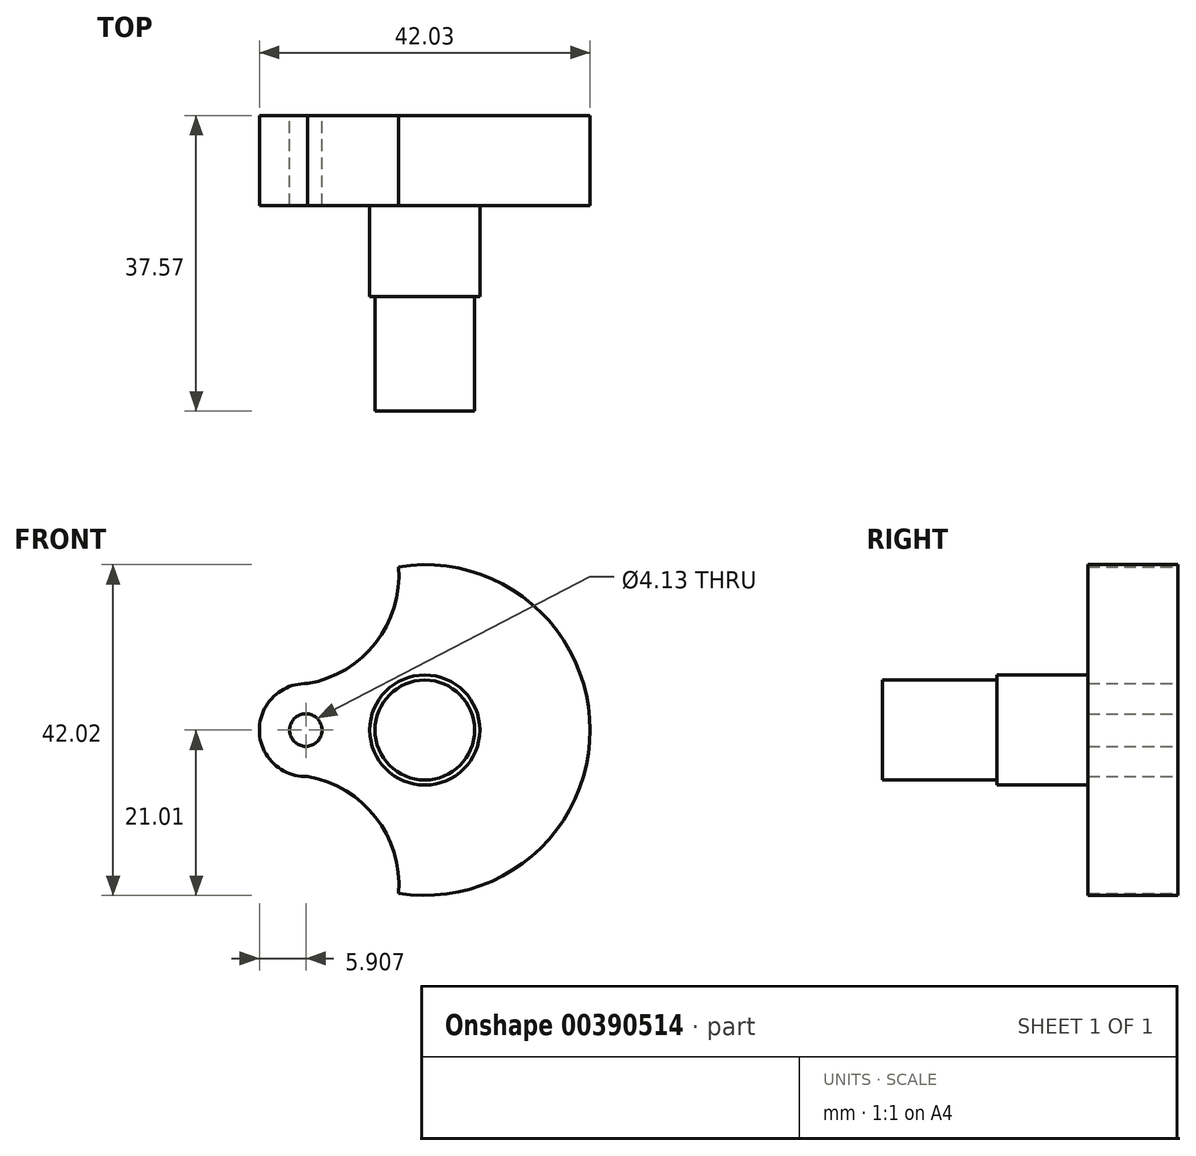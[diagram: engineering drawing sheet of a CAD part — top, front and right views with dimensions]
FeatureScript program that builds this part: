
annotation { "Feature Type Name" : "Feature", "Feature Type Description" : "" }
export const myFeature = defineFeature(function(context is Context, id is Id, definition is map)
    precondition{}
    {
        {
            var Q0;
            Q0=qCreatedBy(makeId("Front.planeOp"),FACE);
            var sketch = newSketch(context, id + "F0", { "sketchPlane" : qUnion([Q0])});
            skArc(sketch, "E0", {"start": v(-3.32, -20.74) * mm, "mid": v(21, 0) * mm, "end": v(-3.32, 20.74) * mm});
            skPoint(sketch, "E1", {"position": v(-15.11, 0) * mm});
            skArc(sketch, "E2", {"start": v(-14.89, 5.9) * mm, "mid": v(-21.02, 0) * mm, "end": v(-14.89, -5.9) * mm});
            skArc(sketch, "E3", {"start": v(-3.32, -20.74) * mm, "mid": v(-6.8, -10.42) * mm, "end": v(-16.61, -5.71) * mm});
            skPoint(sketch, "E3.first.point", {"position": v(-14.89, -5.9) * mm});
            skPoint(sketch, "E3.second.point", {"position": v(-12.16, -32.72) * mm});
            skPoint(sketch, "E3.third.point", {"position": v(-16.61, -5.71) * mm});
            skArc(sketch, "E4.MirrorCS", {"start": v(-3.32, 20.74) * mm, "mid": v(-6.8, 10.42) * mm, "end": v(-16.61, 5.71) * mm});
            skArc(sketch, "E5.trimOffspring", {"start": v(-21, 0.46) * mm, "mid": v(-21, 0) * mm, "end": v(-21, -0.46) * mm});
            skCircle(sketch, "E6", {"center": v(-15.11, 0) * mm, "radius": 2.07 * mm});
            skCircle(sketch, "E7", {"center": v(0, 0) * mm, "radius": 7 * mm});
            skCircle(sketch, "E8", {"center": v(0, 0) * mm, "radius": 6.34 * mm});
            skSolve(sketch);
        }
        {
            var Q0;
            Q0=qSketchRegion(id+"F0",true);
            extrude(context, id + "F1", {"entities" : qUnion([Q0]), "depth" : 11.43 * mm});
        }
        {
            var Q0;
            Q0=makeQuery(id+"F0.imprint","IMPRINT",FACE,{"disambiguationData":[TD([[makeQuery(id+"F0.imprint","IMPRINT",EDGE,{"derivedFrom":sQuery(id+"F0.wireOp",EDGE,"E7")}),1.0]])]});
            extrude(context, id + "F2", {"entities" : qUnion([Q0]), "operationType" : NewBodyOperationType.ADD, "depth" : 23.01 * mm});
        }
        {
            var Q0;
            Q0=makeQuery(id+"F0.imprint","IMPRINT",FACE,{"disambiguationData":[TD([[makeQuery(id+"F0.imprint","IMPRINT",EDGE,{"derivedFrom":sQuery(id+"F0.wireOp",EDGE,"E8")}),1.0]])]});
            extrude(context, id + "F3", {"entities" : qUnion([Q0]), "operationType" : NewBodyOperationType.ADD, "depth" : 37.57 * mm});
        }
    });
